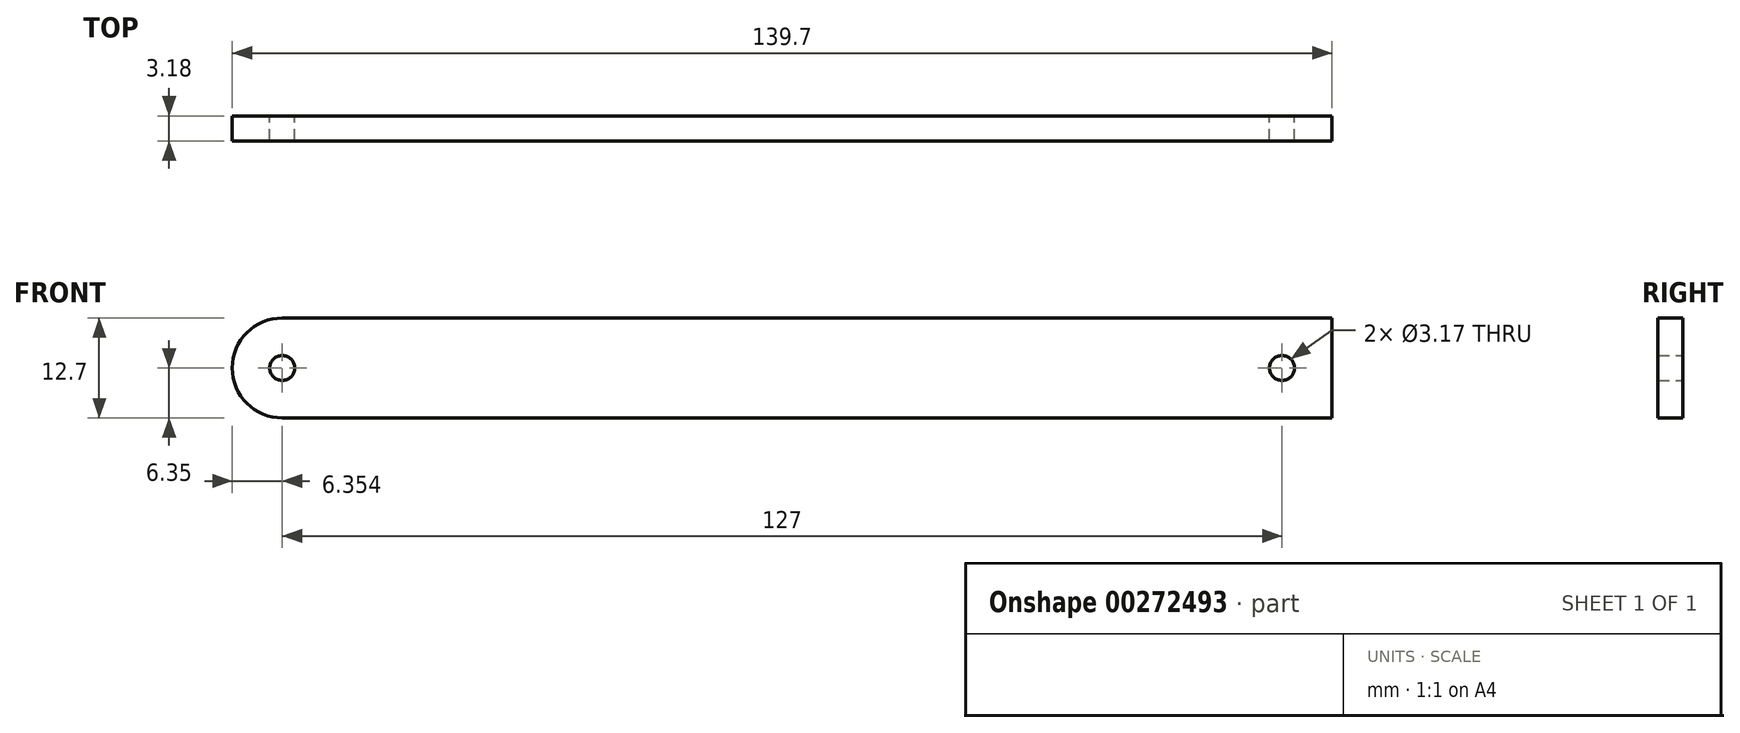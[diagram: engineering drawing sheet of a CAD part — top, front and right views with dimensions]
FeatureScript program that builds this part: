
annotation { "Feature Type Name" : "Feature", "Feature Type Description" : "" }
export const myFeature = defineFeature(function(context is Context, id is Id, definition is map)
    precondition{}
    {
        {
            var Q0;
            Q0=qCreatedBy(makeId("Front.planeOp"),FACE);
            var sketch = newSketch(context, id + "F0", { "sketchPlane" : qUnion([Q0])});
            skLineSegment(sketch, "E0", {"start": v(68.74, 12.7) * mm, "end": v(68.74, 0) * mm});
            skLineSegment(sketch, "E1", {"start": v(-70.96, 6.35) * mm, "end": v(-70.96, 6.35) * mm});
            skLineSegment(sketch, "E2", {"start": v(-64.6, 12.7) * mm, "end": v(68.74, 12.7) * mm});
            skLineSegment(sketch, "E3", {"start": v(-64.6, 0) * mm, "end": v(68.74, 0) * mm});
            skCircle(sketch, "E4", {"center": v(-64.6, 6.35) * mm, "radius": 1.59 * mm});
            skPoint(sketch, "E5.visualSharp", {"position": v(-70.96, 12.7) * mm});
            skArc(sketch, "E5.filletArc", {"start": v(-64.6, 12.7) * mm, "mid": v(-69.1, 10.84) * mm, "end": v(-70.96, 6.35) * mm});
            skPoint(sketch, "E6.visualSharp", {"position": v(-70.96, 0) * mm});
            skArc(sketch, "E6.filletArc", {"start": v(-70.96, 6.35) * mm, "mid": v(-69.1, 1.86) * mm, "end": v(-64.6, 0) * mm});
            skPoint(sketch, "E7.trimOffspring.end.orphan", {"position": v(68.74, 6.35) * mm});
            skPoint(sketch, "E8.orphan", {"position": v(-70.96, 6.35) * mm});
            skCircle(sketch, "E9", {"center": v(62.4, 6.35) * mm, "radius": 1.59 * mm});
            skLineSegment(sketch, "E10", {"start": v(-70.96, 6.35) * mm, "end": v(68.74, 6.35) * mm});
            skSolve(sketch);
        }
        {
            var Q0;
            Q0 = qSketchRegion(id + "F0", true);
            extrude(context, id + "F1", {"entities" : qUnion([Q0]), "depth" : 1.59 * mm, "hasSecondDirection" : true, "secondDirectionOppositeDirection" : true, "secondDirectionDepth" : 1.59 * mm});
        }
    });
